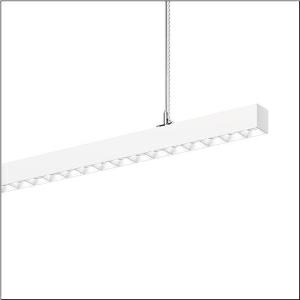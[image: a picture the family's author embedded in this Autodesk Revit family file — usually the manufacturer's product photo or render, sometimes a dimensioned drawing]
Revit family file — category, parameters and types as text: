
# Revit family: silica_r__21_51mx35da47wb_183f
name_source: partatom
category: Lighting Fixtures
units: mm (PartAtom-declared; Revit-internal decimal feet)

## family parameters
Cut with Voids When Loaded = No
Host = Face
Light Source = No
Part Type = Normal
Room Calculation Point = No
Round Connector Dimension = Use Diameter
Shared = No

## types (1)
- --- (1 x LED, 7080 lm, 40.6 W, 4000K)
    Apparent Load = 41 VA
    CIE Flux Codes = 84 98 100 61 100
    Color Rendering = 80
    Color Temperature = 4000K
    Default Elevation = 1800 mm
    Description = Silica® 21, office luminaire, primary light control with darklight reflector, of PMMA, white, CAT 2 (L<= 3000cd/m²), light emission: direct/indirect distribution, primary light characteristic: symmetric, installation type: suspended mounting, LED, rated luminous flux: 7.080lm, luminous efficacy: 174lm/W, light colour: 840, colour temperature: 4000K, with terminal, 3+2-pole, max. 2.5mm², mains connection: 220..240V, AC, 50/60Hz, rated input power: 40.6W, luminaire housing, of aluminium, traffic white (RAL 9016), length: 1.204mm, width: 53mm, height: 53mm, protection rating (complete): IP20, insulation class (complete): insulation class I (protective earthing), certification: CE, permissible operating ambient temperature: 0..+35°C, standard: EN 50419, packaging unit: 1 piece
    Height = 53 mm
    Lamp = 1 x LED
    Lamp Light Flux = 7080 lm
    Lamp Power = 40.6 W
    Lamp count = 1
    Length = 1204 mm
    Luminous efficacy = 174 lm/W
    Manufacturer = Siteco
    ModVariant = No
    Model = 51MX35DA47WB
    Mounting Place = Ceiling
    Mounting Type = Pendant
    Number of Poles = 1
    OnlyDefault = Yes
    Power Factor = 1
    Product Name = Silica® 21
    Product group = office luminaire | ceiling pendant
    ProductGroupID = 902
    Protection Class = Protection class I
    Protection Degree = IP 20
    RLX_Detail_Level = 1
    RLX_Emergency_Light_Flux = 0 lm
    RLX_Emergency_Type = 0
    RLX_Emergency_Type_DB = No
    RlxData = <blob elided: 40933 chars, md5=7f020ad7>
    Socket = socket
    Standby Power = 0 W
    System Light Flux = 7080 lm
    System Power = 41 W
    Type Comments = factory setting: luminous flux: 100 % | dim-lin: 254 | 339 mA
    Type Image = l_1313634.jpg
    URL = http://relux.com
    VarID = @adj_069367
    Voltage = 0 V
    Weight = 0.00 kg
    Width = 53 mm

## geometry (parser evidence)
native form markers: Blend x4, Sweep x11
no freeform markers — native parametric forms only
